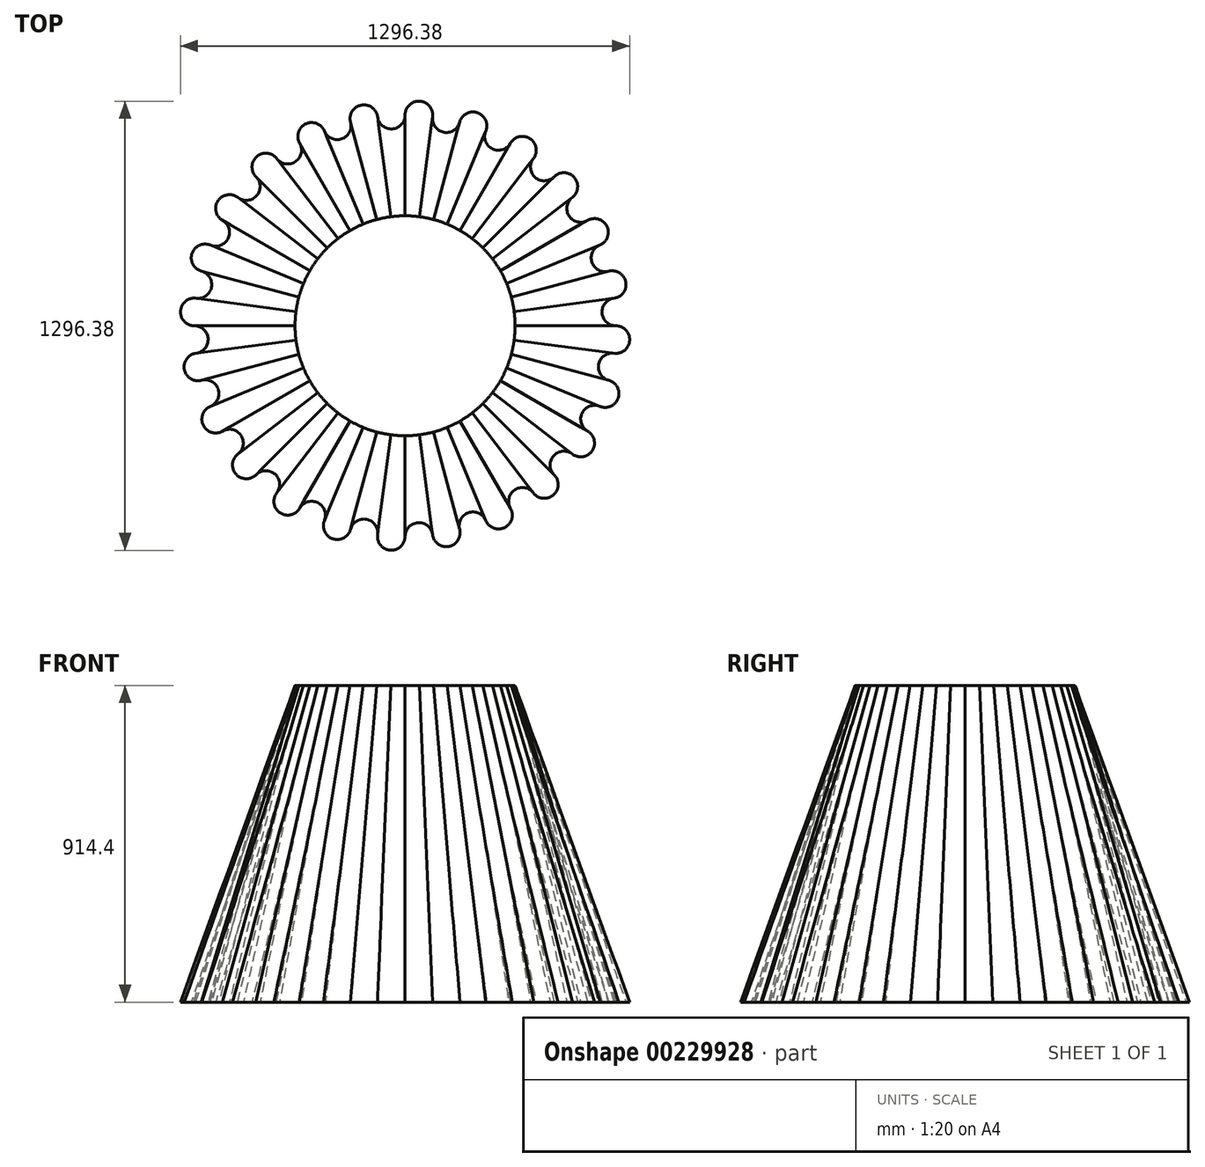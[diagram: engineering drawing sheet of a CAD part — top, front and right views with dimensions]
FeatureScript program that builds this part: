
annotation { "Feature Type Name" : "Feature", "Feature Type Description" : "" }
export const myFeature = defineFeature(function(context is Context, id is Id, definition is map)
    precondition{}
    {
        {
            var Q0;
            Q0=qCreatedBy(makeId("Top.planeOp"),FACE);
            var sketch = newSketch(context, id + "F0", { "sketchPlane" : qUnion([Q0])});
            skCircle(sketch, "E0", {"center": v(0, 0) * mm, "radius": 609.6 * mm, "construction": true});
            skLineSegment(sketch, "E1", {"start": v(0, -609.6) * mm, "end": v(0, 609.6) * mm, "construction": true});
            skLineSegment(sketch, "E2", {"start": v(609.6, 0) * mm, "end": v(-609.6, 0) * mm, "construction": true});
            skArc(sketch, "E3.2.0", {"start": v(-604.38, 79.57) * mm, "mid": v(-558.76, 111.14) * mm, "end": v(-588.83, 157.78) * mm});
            skArc(sketch, "E3.2.1", {"start": v(-604.38, 79.57) * mm, "mid": v(-648.1, 42.48) * mm, "end": v(-609.6, 0) * mm});
            skLineSegment(sketch, "E4", {"start": v(-588.83, 157.78) * mm, "end": v(-604.38, 79.57) * mm, "construction": true});
            skLineSegment(sketch, "E5", {"start": v(-609.6, 0) * mm, "end": v(-604.38, 79.57) * mm, "construction": true});
            skLineSegment(sketch, "E6", {"start": v(-588.83, 157.78) * mm, "end": v(0, 0) * mm, "construction": true});
            skArc(sketch, "E7.1.0", {"start": v(-604.38, -79.57) * mm, "mid": v(-568.49, -37.26) * mm, "end": v(-609.6, 0) * mm});
            skArc(sketch, "E7.1.1", {"start": v(-604.38, -79.57) * mm, "mid": v(-637.01, -126.7) * mm, "end": v(-588.83, -157.78) * mm});
            skArc(sketch, "E7.2.0", {"start": v(-563.2, -233.28) * mm, "mid": v(-539.47, -183.13) * mm, "end": v(-588.83, -157.78) * mm});
            skArc(sketch, "E7.2.1", {"start": v(-563.2, -233.28) * mm, "mid": v(-582.51, -287.26) * mm, "end": v(-527.93, -304.8) * mm});
            skArc(sketch, "E7.3.0", {"start": v(-483.63, -371.1) * mm, "mid": v(-473.7, -316.51) * mm, "end": v(-527.93, -304.8) * mm});
            skArc(sketch, "E7.3.1", {"start": v(-483.63, -371.1) * mm, "mid": v(-488.31, -428.24) * mm, "end": v(-431.05, -431.05) * mm});
            skArc(sketch, "E7.4.0", {"start": v(-371.1, -483.63) * mm, "mid": v(-375.64, -428.33) * mm, "end": v(-431.05, -431.05) * mm});
            skArc(sketch, "E7.4.1", {"start": v(-371.1, -483.63) * mm, "mid": v(-360.84, -540.03) * mm, "end": v(-304.8, -527.93) * mm});
            skArc(sketch, "E7.5.0", {"start": v(-233.28, -563.2) * mm, "mid": v(-251.98, -510.96) * mm, "end": v(-304.8, -527.93) * mm});
            skArc(sketch, "E7.5.1", {"start": v(-233.28, -563.2) * mm, "mid": v(-208.77, -615.02) * mm, "end": v(-157.78, -588.83) * mm});
            skArc(sketch, "E7.6.0", {"start": v(-79.57, -604.38) * mm, "mid": v(-111.14, -558.76) * mm, "end": v(-157.78, -588.83) * mm});
            skArc(sketch, "E7.6.1", {"start": v(-79.57, -604.38) * mm, "mid": v(-42.48, -648.1) * mm, "end": v(0, -609.6) * mm});
            skArc(sketch, "E7.7.0", {"start": v(79.57, -604.38) * mm, "mid": v(37.26, -568.49) * mm, "end": v(0, -609.6) * mm});
            skArc(sketch, "E7.7.1", {"start": v(79.57, -604.38) * mm, "mid": v(126.7, -637.01) * mm, "end": v(157.78, -588.83) * mm});
            skArc(sketch, "E7.8.0", {"start": v(233.28, -563.2) * mm, "mid": v(183.13, -539.47) * mm, "end": v(157.78, -588.83) * mm});
            skArc(sketch, "E7.8.1", {"start": v(233.28, -563.2) * mm, "mid": v(287.26, -582.51) * mm, "end": v(304.8, -527.93) * mm});
            skArc(sketch, "E7.9.0", {"start": v(371.1, -483.63) * mm, "mid": v(316.51, -473.7) * mm, "end": v(304.8, -527.93) * mm});
            skArc(sketch, "E7.9.1", {"start": v(371.1, -483.63) * mm, "mid": v(428.24, -488.31) * mm, "end": v(431.05, -431.05) * mm});
            skArc(sketch, "E7.10.0", {"start": v(483.63, -371.1) * mm, "mid": v(428.33, -375.64) * mm, "end": v(431.05, -431.05) * mm});
            skArc(sketch, "E7.10.1", {"start": v(483.63, -371.1) * mm, "mid": v(540.03, -360.84) * mm, "end": v(527.93, -304.8) * mm});
            skArc(sketch, "E7.11.0", {"start": v(563.2, -233.28) * mm, "mid": v(510.96, -251.98) * mm, "end": v(527.93, -304.8) * mm});
            skArc(sketch, "E7.11.1", {"start": v(563.2, -233.28) * mm, "mid": v(615.02, -208.77) * mm, "end": v(588.83, -157.78) * mm});
            skArc(sketch, "E7.12.0", {"start": v(604.38, -79.57) * mm, "mid": v(558.76, -111.14) * mm, "end": v(588.83, -157.78) * mm});
            skArc(sketch, "E7.12.1", {"start": v(604.38, -79.57) * mm, "mid": v(648.1, -42.48) * mm, "end": v(609.6, 0) * mm});
            skArc(sketch, "E7.13.0", {"start": v(604.38, 79.57) * mm, "mid": v(568.49, 37.26) * mm, "end": v(609.6, 0) * mm});
            skArc(sketch, "E7.13.1", {"start": v(604.38, 79.57) * mm, "mid": v(637.01, 126.7) * mm, "end": v(588.83, 157.78) * mm});
            skArc(sketch, "E7.14.0", {"start": v(563.2, 233.28) * mm, "mid": v(539.47, 183.13) * mm, "end": v(588.83, 157.78) * mm});
            skArc(sketch, "E7.14.1", {"start": v(563.2, 233.28) * mm, "mid": v(582.51, 287.26) * mm, "end": v(527.93, 304.8) * mm});
            skArc(sketch, "E7.15.0", {"start": v(483.63, 371.1) * mm, "mid": v(473.7, 316.51) * mm, "end": v(527.93, 304.8) * mm});
            skArc(sketch, "E7.15.1", {"start": v(483.63, 371.1) * mm, "mid": v(488.31, 428.24) * mm, "end": v(431.05, 431.05) * mm});
            skArc(sketch, "E7.16.0", {"start": v(371.1, 483.63) * mm, "mid": v(375.64, 428.33) * mm, "end": v(431.05, 431.05) * mm});
            skArc(sketch, "E7.16.1", {"start": v(371.1, 483.63) * mm, "mid": v(360.84, 540.03) * mm, "end": v(304.8, 527.93) * mm});
            skArc(sketch, "E7.17.0", {"start": v(233.28, 563.2) * mm, "mid": v(251.98, 510.96) * mm, "end": v(304.8, 527.93) * mm});
            skArc(sketch, "E7.17.1", {"start": v(233.28, 563.2) * mm, "mid": v(208.77, 615.02) * mm, "end": v(157.78, 588.83) * mm});
            skArc(sketch, "E7.18.0", {"start": v(79.57, 604.38) * mm, "mid": v(111.14, 558.76) * mm, "end": v(157.78, 588.83) * mm});
            skArc(sketch, "E7.18.1", {"start": v(79.57, 604.38) * mm, "mid": v(42.48, 648.1) * mm, "end": v(0, 609.6) * mm});
            skArc(sketch, "E7.19.0", {"start": v(-79.57, 604.38) * mm, "mid": v(-37.26, 568.49) * mm, "end": v(0, 609.6) * mm});
            skArc(sketch, "E7.19.1", {"start": v(-79.57, 604.38) * mm, "mid": v(-126.7, 637.01) * mm, "end": v(-157.78, 588.83) * mm});
            skArc(sketch, "E7.20.0", {"start": v(-233.28, 563.2) * mm, "mid": v(-183.13, 539.47) * mm, "end": v(-157.78, 588.83) * mm});
            skArc(sketch, "E7.20.1", {"start": v(-233.28, 563.2) * mm, "mid": v(-287.26, 582.51) * mm, "end": v(-304.8, 527.93) * mm});
            skArc(sketch, "E7.21.0", {"start": v(-371.1, 483.63) * mm, "mid": v(-316.51, 473.7) * mm, "end": v(-304.8, 527.93) * mm});
            skArc(sketch, "E7.21.1", {"start": v(-371.1, 483.63) * mm, "mid": v(-428.24, 488.31) * mm, "end": v(-431.05, 431.05) * mm});
            skArc(sketch, "E7.22.0", {"start": v(-483.63, 371.1) * mm, "mid": v(-428.33, 375.64) * mm, "end": v(-431.05, 431.05) * mm});
            skArc(sketch, "E7.22.1", {"start": v(-483.63, 371.1) * mm, "mid": v(-540.03, 360.84) * mm, "end": v(-527.93, 304.8) * mm});
            skArc(sketch, "E7.23.0", {"start": v(-563.2, 233.28) * mm, "mid": v(-510.96, 251.98) * mm, "end": v(-527.93, 304.8) * mm});
            skArc(sketch, "E7.23.1", {"start": v(-563.2, 233.28) * mm, "mid": v(-615.02, 208.77) * mm, "end": v(-588.83, 157.78) * mm});
            skSolve(sketch);
        }
        {
            var Q0;
            Q0=qCreatedBy(makeId("Top.planeOp"),FACE);
            cPlane(context, id + "F1", {"entities" : qUnion([Q0]), "cplaneType" : CPlaneType.OFFSET, "offset" : 914.4 * mm, "width" : 152.4 * mm, "height" : 152.4 * mm});
        }
        {
            var Q0;
            Q0=qCreatedBy(id+"F1.planeOp",FACE);
            var sketch = newSketch(context, id + "F2", { "sketchPlane" : qUnion([Q0])});
            skCircle(sketch, "E8", {"center": v(0, 0) * mm, "radius": 317.5 * mm});
            skSolve(sketch);
        }
        {
            var Q0;
            Q0=qCreatedBy(makeId("Right.planeOp"),FACE);
            var sketch = newSketch(context, id + "F3", { "sketchPlane" : qUnion([Q0])});
            skArc(sketch, "E9", {"start": v(393.41, 248) * mm, "mid": v(463.35, 89.97) * mm, "end": v(610.89, 0) * mm});
            skLineSegment(sketch, "E10", {"start": v(317.5, 914.4) * mm, "end": v(393.41, 248) * mm});
            skPoint(sketch, "E11", {"position": v(393.41, 914.4) * mm});
            skSolve(sketch);
        }
        {
            var Q0;
            Q0=makeQuery(id+"F0.imprint","IMPRINT",FACE,{"disambiguationData":[TD([[makeQuery(id+"F0.imprint","IMPRINT",EDGE,{"derivedFrom":sQuery(id+"F0.wireOp",EDGE,"E3.2.0")}),-1.0]])]});
            var Q1;
            Q1=makeQuery(id+"F2.imprint","IMPRINT",FACE,{"disambiguationData":[TD([[makeQuery(id+"F2.imprint","IMPRINT",EDGE,{"derivedFrom":sQuery(id+"F2.wireOp",EDGE,"E8")}),1.0]])]});
            var Q2;
            Q2=sQuery(id+"F3.wireOp",VERTEX,"E10.start");
            var Q3;
            Q3=sQuery(id+"F3.wireOp",VERTEX,"E10.end");
            var Q4;
            Q4=sQuery(id+"F3.wireOp",VERTEX,"E9.end");
            loft(context, id + "F4", {"sheetProfilesArray" : [{ "sheetProfileEntities" : qUnion([Q0]) }, { "sheetProfileEntities" : qUnion([Q1]) }], "connections" : [{ "connectionEntities" : qUnion([Q2, Q3, Q4]), "connectionEdgeQueries" : qUnion([]), "connectionEdgeParameters" : [] }]});
        }
    });
